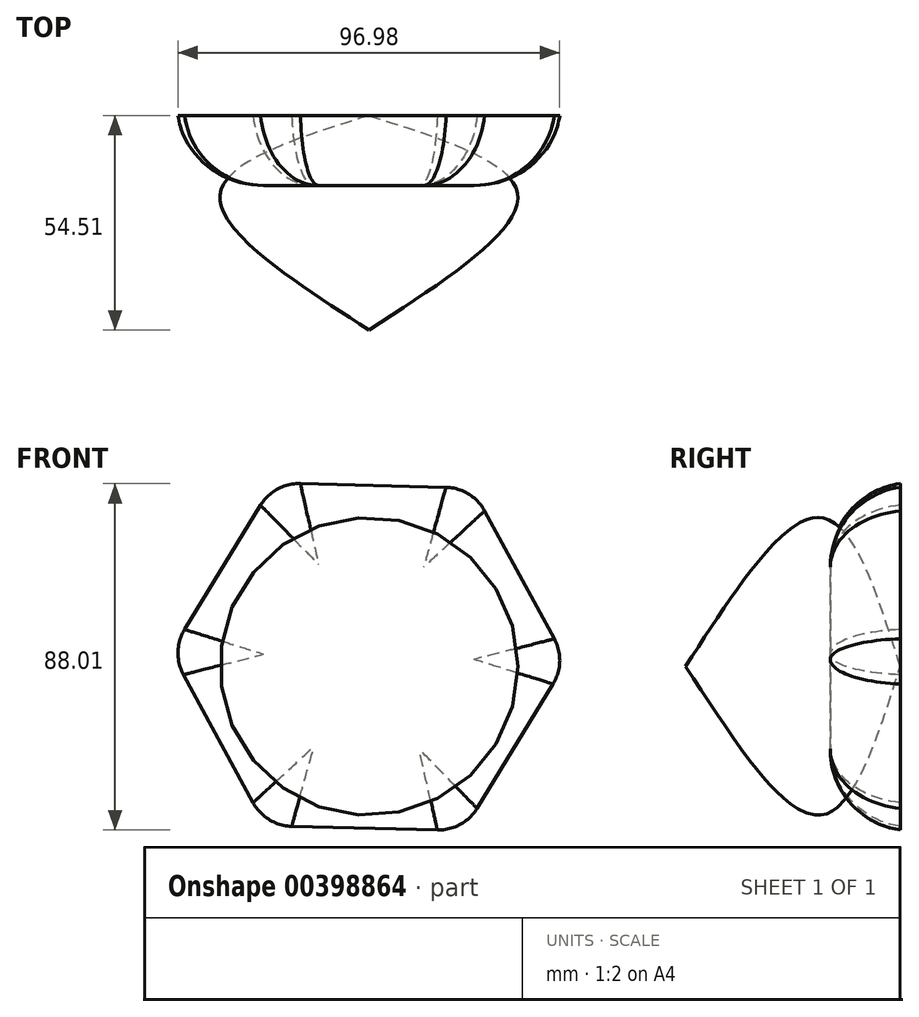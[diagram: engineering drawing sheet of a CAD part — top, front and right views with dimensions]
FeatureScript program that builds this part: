
annotation { "Feature Type Name" : "Feature", "Feature Type Description" : "" }
export const myFeature = defineFeature(function(context is Context, id is Id, definition is map)
    precondition{}
    {
        {
            var Q0;
            Q0=qCreatedBy(makeId("Top.planeOp"),FACE);
            var sketch = newSketch(context, id + "F0", { "sketchPlane" : qUnion([Q0])});
            skLineSegment(sketch, "E0", {"start": v(0, 0) * mm, "end": v(0, -77.87) * mm});
            skFitSpline(sketch, "E1", {"points": [v(0, 0) * mm, v(53.99, -28.62) * mm, v(0, -77.87) * mm], "startDerivative": vector(164.7, -51.71) * mm, "endDerivative": vector(-159.86, -103.26) * mm});
            skSolve(sketch);
        }
        {
            var Q0;
            Q0=makeQuery(id+"F0.imprint","IMPRINT",FACE,{"disambiguationData":[TD([[makeQuery(id+"F0.imprint","IMPRINT",EDGE,{"derivedFrom":sQuery(id+"F0.wireOp",EDGE,"E0")}),1.0]])]});
            var Q1;
            Q1=sQuery(id+"F0.wireOp",EDGE,"E0");
            revolve(context, id + "F1", {"entities" : qUnion([Q0]), "axis" : qUnion([Q1]), "revolveType" : RevolveType.FULL});
        }
        {
            var Q0;
            Q0=qCreatedBy(makeId("Front.planeOp"),FACE);
            var sketch = newSketch(context, id + "F2", { "sketchPlane" : qUnion([Q0])});
            skCircle(sketch, "E2.cCircle", {"center": v(0, 3.47) * mm, "radius": 62.21 * mm, "construction": true});
            skLineSegment(sketch, "E2.0", {"start": v(71.81, 1.66) * mm, "end": v(34.34, -59.63) * mm});
            skLineSegment(sketch, "E2.1", {"start": v(34.34, -59.63) * mm, "end": v(-37.47, -57.82) * mm});
            skLineSegment(sketch, "E2.2", {"start": v(-37.47, -57.82) * mm, "end": v(-71.81, 5.27) * mm});
            skLineSegment(sketch, "E2.3", {"start": v(-71.81, 5.27) * mm, "end": v(-34.34, 66.56) * mm});
            skLineSegment(sketch, "E2.4", {"start": v(-34.34, 66.56) * mm, "end": v(37.47, 64.75) * mm});
            skLineSegment(sketch, "E2.5", {"start": v(37.47, 64.75) * mm, "end": v(71.81, 1.66) * mm});
            skPoint(sketch, "E2.0.midPoint", {"position": v(53.08, -28.99) * mm});
            skSolve(sketch);
        }
        {
            var Q0;
            Q0 = qSketchRegion(id + "F2", true);
            extrude(context, id + "F3", {"entities" : qUnion([Q0]), "depth" : 25.4 * mm});
        }
        {
            var Q0;
            Q0=makeQuery(id+"F3.opExtrude","SWEPT_EDGE",EDGE,{"disambiguationData":[OSD([sQuery(id+"F2.wireOp",EDGE,"E2.0"),sQuery(id+"F2.wireOp",EDGE,"E2.1")])]});
            var Q1;
            Q1=makeQuery(id+"F3.opExtrude","SWEPT_EDGE",EDGE,{"disambiguationData":[OSD([sQuery(id+"F2.wireOp",EDGE,"E2.1"),sQuery(id+"F2.wireOp",EDGE,"E2.2")])]});
            var Q2;
            Q2=makeQuery(id+"F3.opExtrude","SWEPT_EDGE",EDGE,{"disambiguationData":[OSD([sQuery(id+"F2.wireOp",EDGE,"E2.2"),sQuery(id+"F2.wireOp",EDGE,"E2.3")])]});
            var Q3;
            Q3=makeQuery(id+"F3.opExtrude","SWEPT_EDGE",EDGE,{"disambiguationData":[OSD([sQuery(id+"F2.wireOp",EDGE,"E2.3"),sQuery(id+"F2.wireOp",EDGE,"E2.4")])]});
            var Q4;
            Q4=makeQuery(id+"F3.opExtrude","SWEPT_EDGE",EDGE,{"disambiguationData":[OSD([sQuery(id+"F2.wireOp",EDGE,"E2.4"),sQuery(id+"F2.wireOp",EDGE,"E2.5")])]});
            var Q5;
            Q5=makeQuery(id+"F3.opExtrude","SWEPT_EDGE",EDGE,{"disambiguationData":[OSD([sQuery(id+"F2.wireOp",EDGE,"E2.0"),sQuery(id+"F2.wireOp",EDGE,"E2.5")])]});
            fillet(context, id + "F4", {"entities" : qUnion([Q0, Q1, Q2, Q3, Q4, Q5]), "radius" : 16.42 * mm, "tangentPropagation" : true, "allowEdgeOverflow" : false});
        }
        {
            var Q0;
            Q0=makeQuery(id+"F3.opExtrude","CAP_EDGE",EDGE,{"disambiguationData":[OSD([sQuery(id+"F2.wireOp",EDGE,"E2.3")])],"isStart":false});
            fillet(context, id + "F5", {"entities" : qUnion([Q0]), "radius" : 29.43 * mm, "tangentPropagation" : true, "allowEdgeOverflow" : false});
        }
        {
            var Q0;
            Q0=makeQuery(id+"F1.opRevolve","SWEPT_BODY",BODY,{"disambiguationData":[OSD([sQuery(id+"F0.wireOp",EDGE,"E0"),sQuery(id+"F0.wireOp",EDGE,"E1")])]});
            var Q1;
            Q1=makeQuery(id+"F3.opExtrude","SWEPT_BODY",BODY,{"disambiguationData":[OSD([sQuery(id+"F2.wireOp",EDGE,"E2.0"),sQuery(id+"F2.wireOp",EDGE,"E2.1"),sQuery(id+"F2.wireOp",EDGE,"E2.2"),sQuery(id+"F2.wireOp",EDGE,"E2.3"),sQuery(id+"F2.wireOp",EDGE,"E2.4"),sQuery(id+"F2.wireOp",EDGE,"E2.5")])]});
            var Q2;
            Q2=sQuery(id+"F0.wireOp",VERTEX,"E0.start");
            transform(context, id + "F6", {"entities" : qUnion([Q0, Q1]), "transformType" : TransformType.SCALE_UNIFORMLY, "scale" : .7, "scalePoint" : qUnion([Q2]), "makeCopy" : false});
        }
    });
